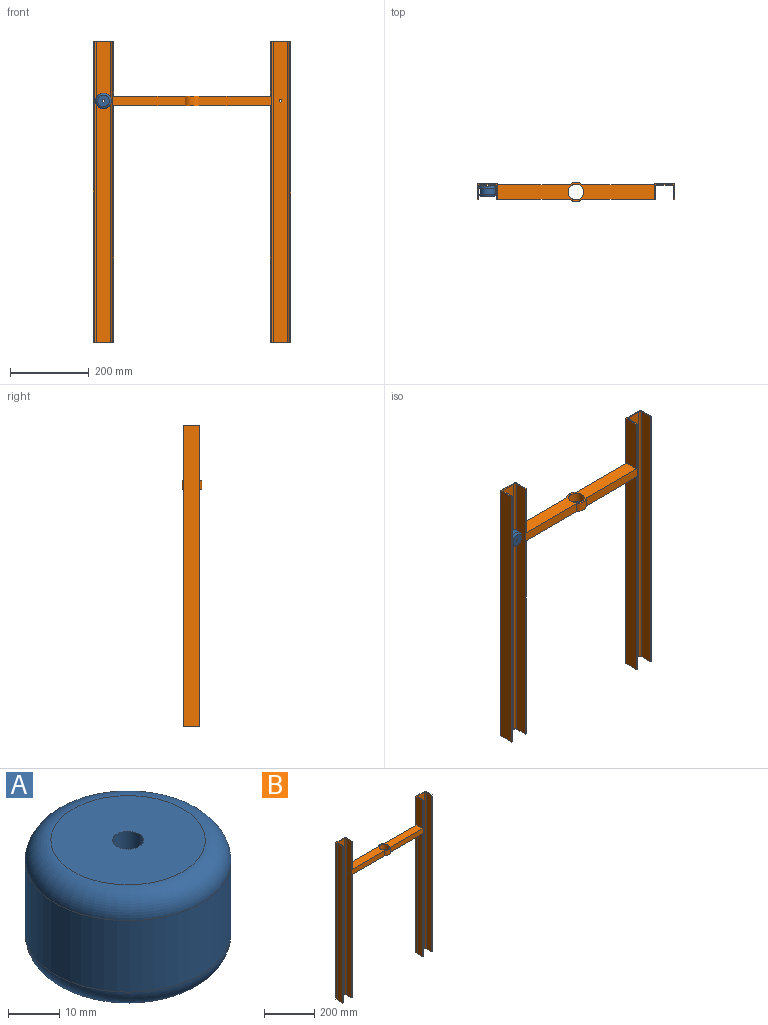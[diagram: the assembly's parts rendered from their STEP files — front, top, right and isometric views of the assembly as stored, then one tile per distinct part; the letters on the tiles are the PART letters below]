
ASSEMBLY  parts=2 mates=1
PART A: 6 faces, bbox 43.3x43.3x27 mm
  f0: cylinder r=3mm len=27mm, axis (0,0,-1), area 508.9mm2, adj f2,f3
  f1: cylinder r=20mm len=40mm, axis (0,0,-1), area 2136.3mm2, adj f4,f5
  f2: plane 30x30mm, normal (0,0,1), area 678.6mm2, adj f0,f5
  f3: plane 30x30mm, normal (0,0,-1), area 678.6mm2, adj f0,f4
  f4: torus R=15mm, axis (0,0,1), area 897.3mm2, adj f1,f3
  f5: torus R=15mm, axis (0,0,1), area 897.3mm2, adj f1,f2
PART B: 33 faces, bbox 502.1x50x763 mm
  f0: plane 763x39mm, normal (1,0,0), area 28857mm2, adj f8,f9,f10,f11,f16,f17,f18
  f1: plane 763x39mm, normal (-1,0,0), area 29757mm2, adj f2,f9,f10,f11
  f2: plane 763x3mm, normal (0,-1,0), area 2289mm2, adj f1,f3,f10,f11
  f3: plane 763x30.5mm, normal (1,0,0), area 23271.5mm2, adj f2,f4,f10,f11
  f4: cylinder r=5.5mm len=763mm, axis (0,0,-1), area 6591.8mm2, adj f3,f5,f10,f11
  f5: plane 763x35.1mm, normal (0,-1,0), area 26753mm2, adj f4,f6,f10,f11,f12
  f6: cylinder r=5.5mm len=763mm, axis (0,0,-1), area 6591.8mm2, adj f5,f7,f10,f11
  f7: plane 763x30.5mm, normal (-1,0,0), area 23271.5mm2, adj f6,f8,f10,f11
  f8: plane 763x184.6mm, normal (0,-1,0), area 6829mm2, adj f0,f7,f10,f11,f13,f17,f18
  f9: plane 763x52.1mm, normal (0,1,0), area 39724mm2, adj f0,f1,f10,f11,f12
  f10: plane 52.1x39mm, normal (0,0,1), area 385.3mm2, adj f0,f1,f2,f3,f4,f5,f6,f7
  f11: plane 52.1x39mm, normal (0,0,-1), area 385.3mm2, adj f0,f1,f2,f3,f4,f5,f6,f7
  f12: cylinder r=3mm len=6mm, axis (0,-1,0), area 56.5mm2, adj f5,f9
  f13: cylinder r=25mm len=34.7mm, axis (0,0,-1), area 958.7mm2, adj f8,f17,f18,f27
  f14: cylinder r=20mm len=40mm, axis (0,0,-1), area 3141.6mm2, adj f17,f18
  f15: cylinder r=25mm len=34.7mm, axis (0,0,-1), area 958.7mm2, adj f16,f17,f18,f32
  f16: plane 181.6x25mm, normal (0,1,0), area 4540mm2, adj f0,f15,f17,f18
  f17: plane 397.9x50mm, normal (0,0,1), area 13401.9mm2, adj f0,f8,f13,f14,f15,f16,f19,f27
  f18: plane 397.9x50mm, normal (0,0,-1), area 13401.9mm2, adj f0,f8,f13,f14,f15,f16,f19,f27
  f19: plane 763x39mm, normal (-1,0,0), area 28857mm2, adj f17,f18,f27,f28,f29,f30,f32
  f20: plane 763x39mm, normal (1,0,0), area 29757mm2, adj f21,f28,f29,f30
  f21: plane 763x3mm, normal (0,-1,0), area 2289mm2, adj f20,f22,f29,f30
  f22: plane 763x30.5mm, normal (-1,0,0), area 23271.5mm2, adj f21,f23,f29,f30
  f23: cylinder r=5.5mm len=763mm, axis (0,0,-1), area 6591.8mm2, adj f22,f24,f29,f30
  f24: plane 763x35.1mm, normal (0,-1,0), area 26753mm2, adj f23,f25,f29,f30,f31
  f25: cylinder r=5.5mm len=763mm, axis (0,0,-1), area 6591.8mm2, adj f24,f26,f29,f30
  f26: plane 763x30.5mm, normal (1,0,0), area 23271.5mm2, adj f25,f27,f29,f30
  f27: plane 763x184.6mm, normal (0,-1,0), area 6829mm2, adj f13,f17,f18,f19,f26,f29,f30
  f28: plane 763x52.1mm, normal (0,1,0), area 39724mm2, adj f19,f20,f29,f30,f31
  f29: plane 52.1x39mm, normal (0,0,1), area 385.3mm2, adj f19,f20,f21,f22,f23,f24,f25,f26
  f30: plane 52.1x39mm, normal (0,0,-1), area 385.3mm2, adj f19,f20,f21,f22,f23,f24,f25,f26
  f31: cylinder r=3mm len=6mm, axis (0,-1,0), area 56.5mm2, adj f24,f28
  f32: plane 181.6x25mm, normal (0,1,0), area 4540mm2, adj f15,f17,f18,f19
PLACE A rot(axis=(-1,0,0),90deg) t=(-2.36,-13.21,-3.51)mm
PLACE B t=(-2.36,6.29,-3.51)mm
MATE revolute A.f0 <-> B.f12  axis (0,1,0) through (-2.36,0.29,-3.51)mm
